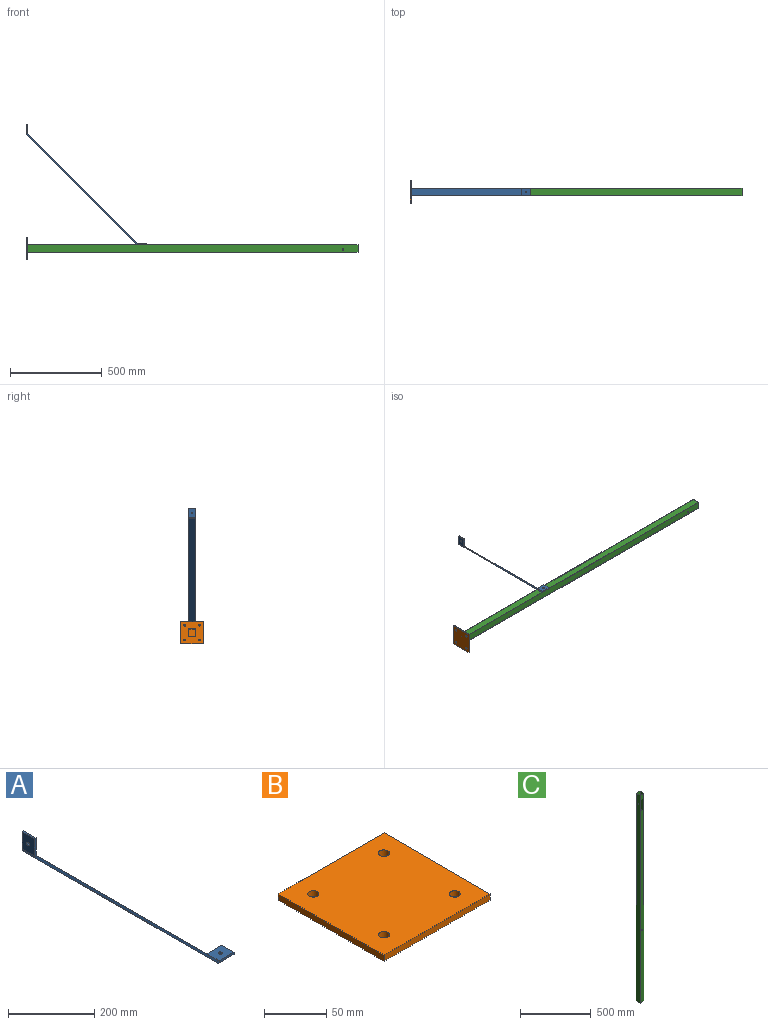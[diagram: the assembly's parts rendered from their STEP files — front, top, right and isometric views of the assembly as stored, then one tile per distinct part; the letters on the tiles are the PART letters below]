
ASSEMBLY  parts=3 mates=5
PART A: 24 faces, bbox 656x40x656 mm
  f0: plane 49.05x6mm, normal (0,1,0), area 294.3mm2, adj f3,f4,f5,f21
  f1: plane 49.05x6mm, normal (0,-1,0), area 294.3mm2, adj f3,f4,f5,f20
  f2: cylinder r=4.5mm len=9mm, axis (-1,0,0), area 169.6mm2, adj f4,f5
  f3: plane 40x6mm, normal (0,0,1), area 240mm2, adj f0,f1,f4,f5
  f4: plane 49.05x40mm, normal (-1,0,0), area 1898.3mm2, adj f0,f1,f2,f3,f22
  f5: plane 49.05x40mm, normal (1,0,0), area 1898.3mm2, adj f0,f1,f2,f3,f23
  f6: plane 602.9x602.9mm, normal (0,1,0), area 5079.7mm2, adj f8,f9,f17,f21
  f7: plane 602.9x602.9mm, normal (0,-1,0), area 5079.7mm2, adj f8,f9,f16,f20
  f8: plane 598.65x598.65mm, normal (-0.71,0,-0.71), area 33864.9mm2, adj f6,f7,f18,f22
  f9: plane 598.65x598.65mm, normal (0.71,0,0.71), area 33864.9mm2, adj f6,f7,f19,f23
  f10: plane 49.05x6mm, normal (0,1,0), area 294.3mm2, adj f11,f14,f15,f17
  f11: plane 40x6mm, normal (1,0,0), area 240mm2, adj f10,f12,f14,f15
  f12: plane 49.05x6mm, normal (0,-1,0), area 294.3mm2, adj f11,f14,f15,f16
  f13: cylinder r=4.5mm len=9mm, axis (0,0,-1), area 169.6mm2, adj f14,f15
  f14: plane 49.05x40mm, normal (0,0,-1), area 1898.3mm2, adj f10,f11,f12,f13,f18
  f15: plane 49.05x40mm, normal (0,0,1), area 1898.3mm2, adj f10,f11,f12,f13,f19
  f16: plane 6.67x5.87mm, normal (0,-1,0), area 25mm2, adj f7,f12,f18,f19
  f17: plane 6.67x5.87mm, normal (0,1,0), area 25mm2, adj f6,f10,f18,f19
  f18: cylinder r=8.3mm len=40mm, axis (0,-1,0), area 260.8mm2, adj f8,f14,f16,f17
  f19: cylinder r=2.3mm len=40mm, axis (0,-1,0), area 72.3mm2, adj f9,f15,f16,f17
  f20: plane 6.67x5.87mm, normal (0,-1,0), area 25mm2, adj f1,f7,f22,f23
  f21: plane 6.67x5.87mm, normal (0,1,0), area 25mm2, adj f0,f6,f22,f23
  f22: cylinder r=8.3mm len=40mm, axis (0,-1,0), area 260.8mm2, adj f4,f8,f20,f21
  f23: cylinder r=2.3mm len=40mm, axis (0,-1,0), area 72.3mm2, adj f5,f9,f20,f21
PART B: 10 faces, bbox 120x120x6 mm
  f0: plane 120x6mm, normal (-1,0,0), area 720mm2, adj f1,f3,f4,f5
  f1: plane 120x6mm, normal (0,-1,0), area 720mm2, adj f0,f2,f4,f5
  f2: plane 120x6mm, normal (1,0,0), area 720mm2, adj f1,f3,f4,f5
  f3: plane 120x6mm, normal (0,1,0), area 720mm2, adj f0,f2,f4,f5
  f4: plane 120x120mm, normal (0,0,1), area 14145.5mm2, adj f0,f1,f2,f3,f6,f7,f8,f9
  f5: plane 120x120mm, normal (0,0,-1), area 14145.5mm2, adj f0,f1,f2,f3,f6,f7,f8,f9
  f6: cylinder r=4.5mm len=9mm, axis (0,0,1), area 169.6mm2, adj f4,f5
  f7: cylinder r=4.5mm len=9mm, axis (0,0,1), area 169.6mm2, adj f4,f5
  f8: cylinder r=4.5mm len=9mm, axis (0,0,1), area 169.6mm2, adj f4,f5
  f9: cylinder r=4.5mm len=9mm, axis (0,0,1), area 169.6mm2, adj f4,f5
PART C: 21 faces, bbox 40x40x1800 mm
  f0: plane 1800x40mm, normal (1,0,0), area 71600mm2, adj f3,f7,f8,f9,f15,f16,f17,f18
  f1: plane 1800x36.8mm, normal (-1,0,0), area 65840mm2, adj f2,f5,f8,f9,f15,f16,f17,f18
  f2: plane 1800x36.8mm, normal (0,1,0), area 63836.4mm2, adj f1,f4,f8,f9,f11,f12,f13,f14
  f3: plane 1800x40mm, normal (0,-1,0), area 69596.4mm2, adj f0,f6,f8,f9,f11,f12,f13,f14
  f4: plane 1800x36.8mm, normal (1,0,0), area 66204.1mm2, adj f2,f5,f8,f9,f10
  f5: plane 1800x36.8mm, normal (0,-1,0), area 66176.4mm2, adj f1,f4,f8,f9,f19
  f6: plane 1800x40mm, normal (-1,0,0), area 71964.1mm2, adj f3,f7,f8,f9,f10
  f7: plane 1800x40mm, normal (0,1,0), area 71936.4mm2, adj f0,f6,f8,f9,f19
  f8: plane 40x40mm, normal (0,0,1), area 245.8mm2, adj f0,f1,f2,f3,f4,f5,f6,f7
  f9: plane 40x40mm, normal (0,0,-1), area 245.8mm2, adj f0,f1,f2,f3,f4,f5,f6,f7
  f10: cylinder r=3.38mm len=6.76mm, axis (-1,0,0), area 34mm2, adj f4,f6
  f11: plane 26x1.6mm, normal (0,0,-1), area 41.6mm2, adj f2,f3,f12,f14
  f12: plane 90x1.6mm, normal (1,0,0), area 144mm2, adj f2,f3,f11,f13
  f13: plane 26x1.6mm, normal (0,0,1), area 41.6mm2, adj f2,f3,f12,f14
  f14: plane 90x1.6mm, normal (-1,0,0), area 144mm2, adj f2,f3,f11,f13
  f15: plane 20x1.6mm, normal (0,1,0), area 32mm2, adj f0,f1,f16,f18
  f16: plane 20x1.6mm, normal (0,0,1), area 32mm2, adj f0,f1,f15,f17
  f17: plane 20x1.6mm, normal (0,-1,0), area 32mm2, adj f0,f1,f16,f18
  f18: plane 20x1.6mm, normal (0,0,-1), area 32mm2, adj f0,f1,f15,f17
  f19: cylinder r=4.5mm len=9mm, axis (0,1,0), area 45.2mm2, adj f5,f7
  f20: cylinder r=4.5mm len=9mm, axis (0,1,0), area 45.2mm2, adj f2,f3
PLACE A t=(-1013.69,409.28,3033.77)mm
PLACE B rot(axis=(0.58,-0.58,-0.58),120deg) t=(-1013.69,449.28,2947.77)mm
PLACE C rot(axis=(0.58,0.58,0.58),120deg) t=(-1013.69,369.28,2987.77)mm fixed
MATE parallel C.f6 <-> B.f2  axis (0,-1,0) through (-114.1,369.28,3007.77)mm
MATE cylindrical C.f19 <-> A.f13  axis (0,0,1) through (-388.69,389.28,3027.77)mm
MATE planar B.f5 <-> C.f9  axis (1,0,0) through (-1013.69,389.28,3007.77)mm
MATE parallel B.f3 <-> C.f7  axis (0,0,1) through (-1016.69,389.28,3067.77)mm
MATE planar A.f13 <-> C.f7  axis (0,0,-1) through (-388.69,389.28,3027.77)mm
